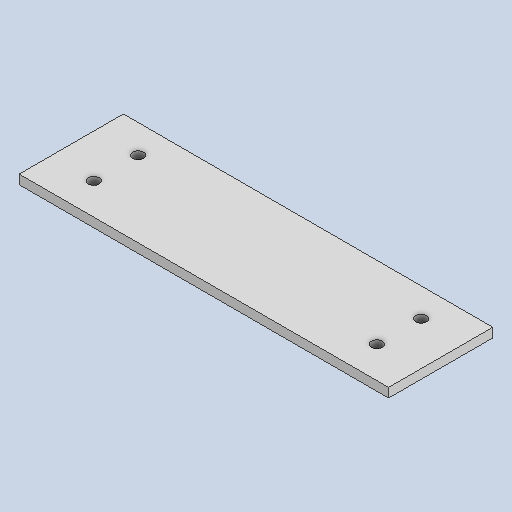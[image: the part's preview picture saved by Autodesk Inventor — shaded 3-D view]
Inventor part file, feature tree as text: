
AUTODESK INVENTOR PART (.ipt)
format: ipt  version: 2023 (Build 270158000, 158)  size: 233,472 bytes
history: native  units: mm
features: other x4, reference x2, extrude x1, sketch x1
ambient origin geometry x8: Origin, YZ Plane, XZ Plane, XY Plane, X Axis, Y Axis, Z Axis, Center Point
bodies: Solid1 (feature_tree)
feature tree (8):
  extrude  "Extrusion1"  Depth=2.5mm
  sketch  "Sketch2"  dims[d0=3.0mm d1=3.0mm d2=76.6mm d3=100.0mm d4=3.0mm d5=3.0mm d6=5.0mm d7=5.0mm d8=2.5mm d9=0.0mm]
  reference  "Reference4"
  reference  "Reference5"
  parser-record x1  (decoder bookkeeping rows leaked as tree rows — omitted from the tree; the rows remain in map.json)
  other  "A.iam"
  other  "A-04:1"
  other  "A-04:2"
note: 1 file-system path scrubbed to <path> (originals preserved in map.json)
